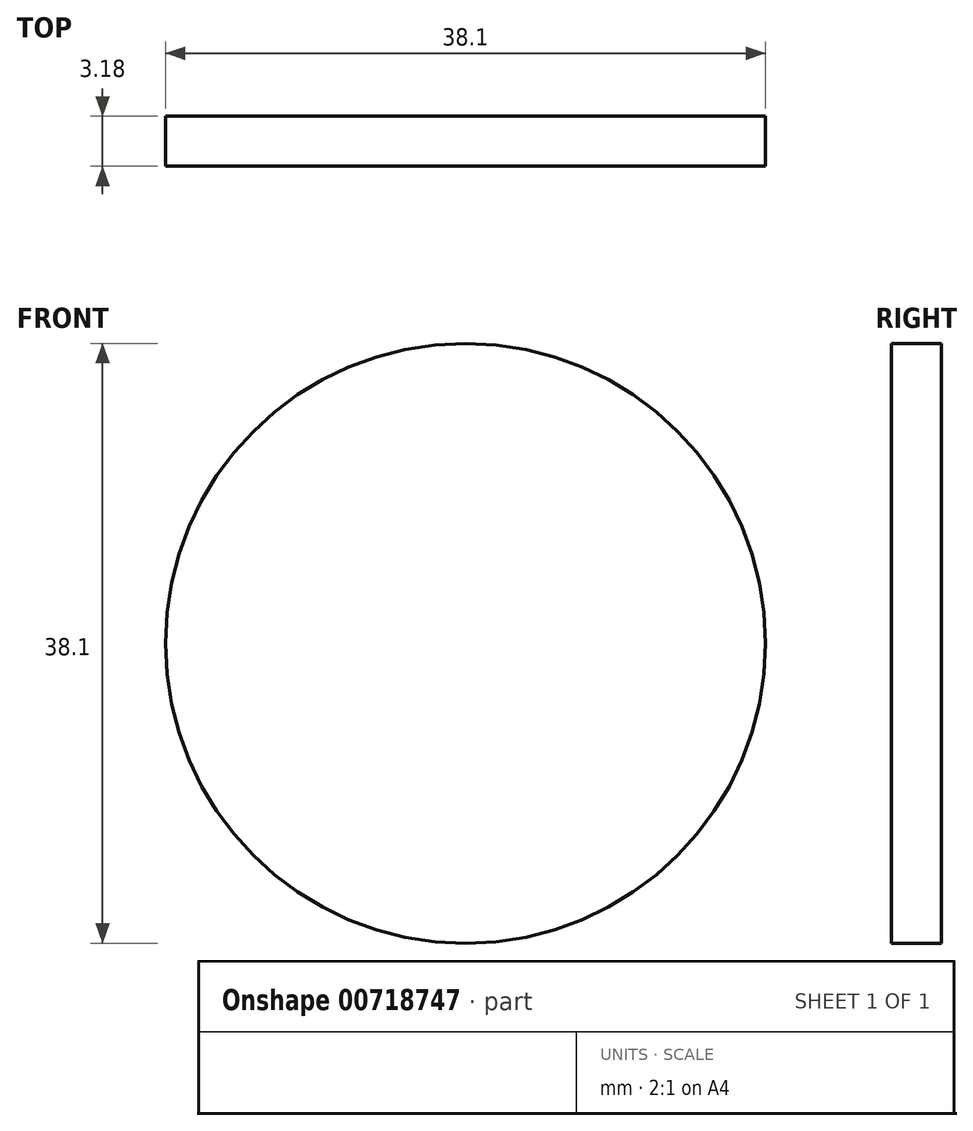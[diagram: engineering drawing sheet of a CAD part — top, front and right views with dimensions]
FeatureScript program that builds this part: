
annotation { "Feature Type Name" : "Feature", "Feature Type Description" : "" }
export const myFeature = defineFeature(function(context is Context, id is Id, definition is map)
    precondition{}
    {
        {
            var Q0;
            Q0=qCreatedBy(makeId("Front.planeOp"),FACE);
            var sketch = newSketch(context, id + "F0", { "sketchPlane" : qUnion([Q0])});
            skPoint(sketch, "E0.middle", {"position": v(0, 0) * mm});
            skCircle(sketch, "E1", {"center": v(0, 0) * mm, "radius": 19.05 * mm});
            skSolve(sketch);
        }
        {
            var Q0;
            Q0=makeQuery(id+"F0.imprint","IMPRINT",FACE,{"disambiguationData":[TD([[makeQuery(id+"F0.imprint","IMPRINT",EDGE,{"derivedFrom":sQuery(id+"F0.wireOp",EDGE,"E1")}),1.0]])]});
            extrude(context, id + "F1", {"entities" : qUnion([Q0]), "depth" : 3.17 * mm, "offsetDistance" : 25.4 * mm});
        }
    });
